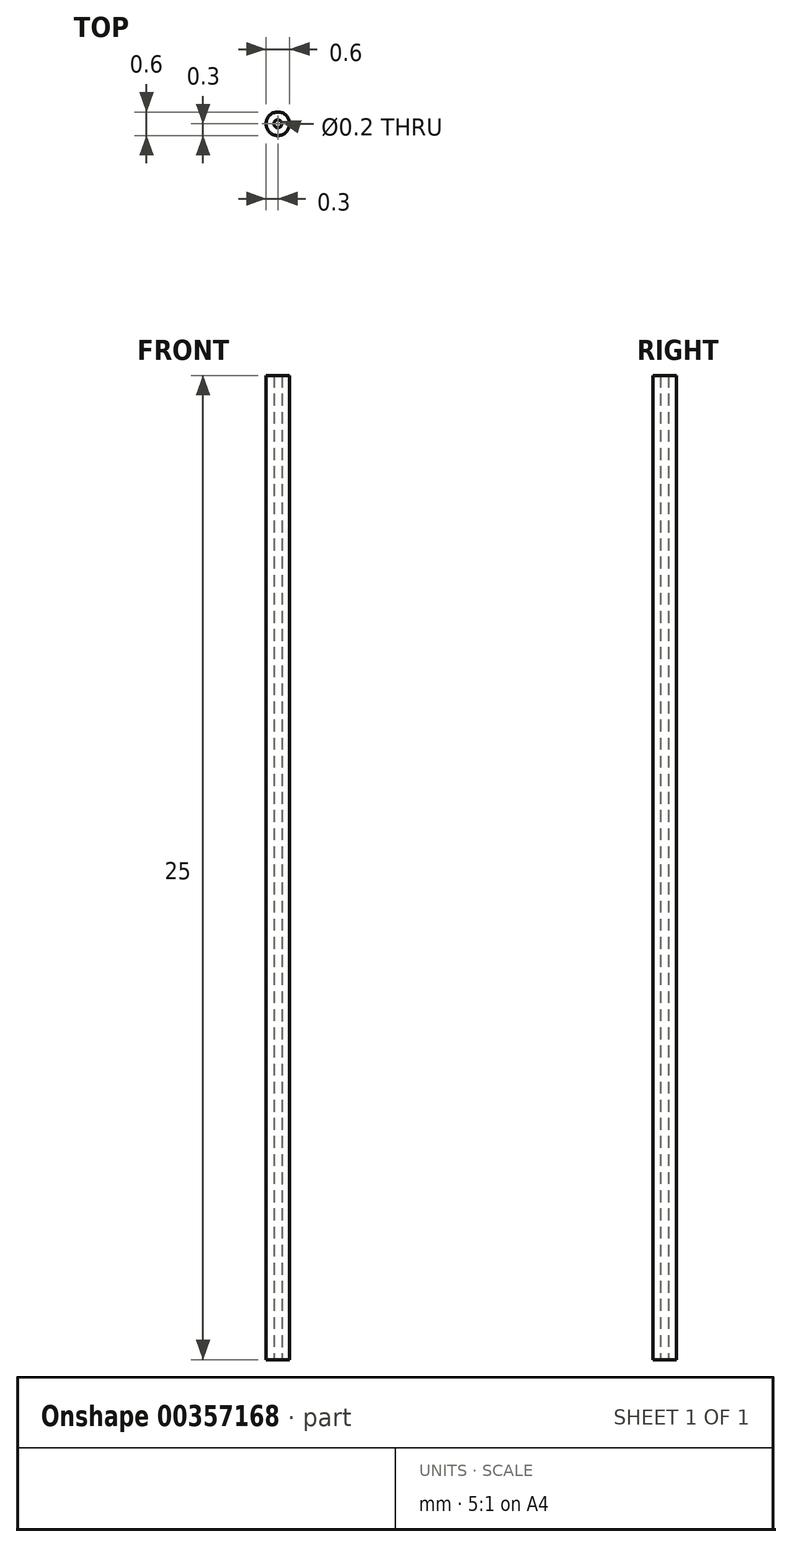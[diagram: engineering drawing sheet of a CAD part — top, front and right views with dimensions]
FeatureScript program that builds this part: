
annotation { "Feature Type Name" : "Feature", "Feature Type Description" : "" }
export const myFeature = defineFeature(function(context is Context, id is Id, definition is map)
    precondition{}
    {
        {
            var Q0;
            Q0=qCreatedBy(makeId("Top.planeOp"),FACE);
            var sketch = newSketch(context, id + "F0", { "sketchPlane" : qUnion([Q0])});
            skCircle(sketch, "E0", {"center": v(0, 0) * mm, "radius": 0.3 * mm});
            skCircle(sketch, "E1", {"center": v(0, 0) * mm, "radius": 0.1 * mm});
            skSolve(sketch);
        }
        {
            var Q0;
            Q0 = qSketchRegion(id + "F0", true);
            extrude(context, id + "F1", {"entities" : qUnion([Q0]), "endBound" : BoundingType.SYMMETRIC, "depth" : 25 * mm});
        }
    });
